# Revit family: 42825
name_source: partatom
category: Lighting Fixtures
revit_build: Autodesk Revit 2018 (Build: 20170223_1515(x64)
units: mm (PartAtom-declared; Revit-internal decimal feet)

## family parameters
Cut with Voids When Loaded = No
Host = Face
Light Source = Yes
OmniClass Number = 23.80.70.00
OmniClass Title = Lighting
Part Type = Normal
Room Calculation Point = No
Round Connector Dimension = Use Diameter
Shared = No

## types (1)
- 0042825 SRT PANEL UGR19 600X600 3600LM 840 LILO
    Apparent Load = 36 VA
    Assembly Code = D5020200
    AssetType = Fixed
    BezelOffset_FEILO = 30 mm  [stored 0.0984252 ft]
    ClassificationName = Uniclass2015
    ClassificationValue = EF_70_80
    Color Filter = 16777215
    Cost = 0 $
    Default Elevation = 1219 mm
    Description = LED Panel with backlit technology, ideal for general indoor lighting applications such as breakout areas, offices and meeting rooms. Extruded aluminium frame, passive cooling. Low glaring UGR<19. RG0, 90 degree beam angle , optical system: PS diffuser with Prismatic finish. Light color temperature: 4000K Neutral White, total system power: 36W , total fixture output: 3600lm, efficacy: 100 lm/W, Ra80 typical, LED chromacity: 3 step MacAdam ellipse (SDCM3), lifespan: 100,000 hours at 70% of the original output (L70B50), IR/UV free light source without heat radiation, operating voltage: 220-240V / 50-60Hz, low flicker, non dimmable driver, electrical protection: Class II. Degree of Protection: IP40/IP20, suitable for indoor environment only. Nominal size: 595x595mm, Loop in / loop out wiring, saftey cables included, 25mm nominal height, White color frame, weight: 1,6Kg.
    Dimming Lamp Color Temperature Shift = <None>
    DocumentationLiterature = http://www.sylvania-lighting.com
    DurationUnit = hours
    ElectricShockClassification = 100
    Emit Shape Visible in Rendering = No
    Emit from Rectangle Length = 566 mm
    Emit from Rectangle Width = 566 mm
    ExpectedLife = 50000
    IfcExportAs = Class II
    IfcExportType = IfcLightFixtureType
    ImpactProtectionIndex = IfcLightFixtureType
    IngressProtection = IfcLightFixtureType
    InputNominalFrequency = 4000
    InputVoltage = 0
    LampColourRenderingIndex = 16500
    LampColourTemperature = LED
    LampMacAdamStep = 80
    LampNominalLuminous = 4000 K
    Length_FEILO = 596 mm  [stored 1.95538 ft]
    LightOutputRatio = LED
    LuminaireType = 0
    ManufacturerName = 100 lm/W
    Material = Feilo Sylvania
    Material_1_FEILO = Body-Sylvania-Start Panel LED DALI-White
    Material_2_FEILO = Diffuser-Sylvania-Start Panel LED DALI
    Material_3_FEILO = <By Category>
    Material_4_FEILO = <By Category>
    Model = START Panel UGR19 600x600 3600Lm 840 LILO
    ModelNumber = 0042825
    ModelReference = START Panel UGR19 600x600 3600Lm 840 LILO
    Name = START Panel UGR19 600x600 3600Lm 840 LILO
    NominalDepth = 596 mm  [stored 1.95538 ft]
    NominalHeight = 25 mm  [stored 0.082021 ft]
    NominalLength = 595 mm  [stored 1.9521 ft]
    Photometric Web File = 0042825.ies
    PowerConsumption = Lighting
    PowerFactor = 0.97
    Tilt Angle = -90.00°
    Type Image = <None>
    TypeName = START Panel UGR19 600x600 3600Lm 840 LILO
    URL = 0.9
    Voltage = 230 V
    WarrantyDescription = http://www.sylvania-lighting.com

note: [stored X ft] marks values corroborated as IEEE doubles in the binary element streams (Revit-internal decimal feet)

## geometry (parser evidence)
native form markers: Sweep x3
no freeform markers — native parametric forms only
